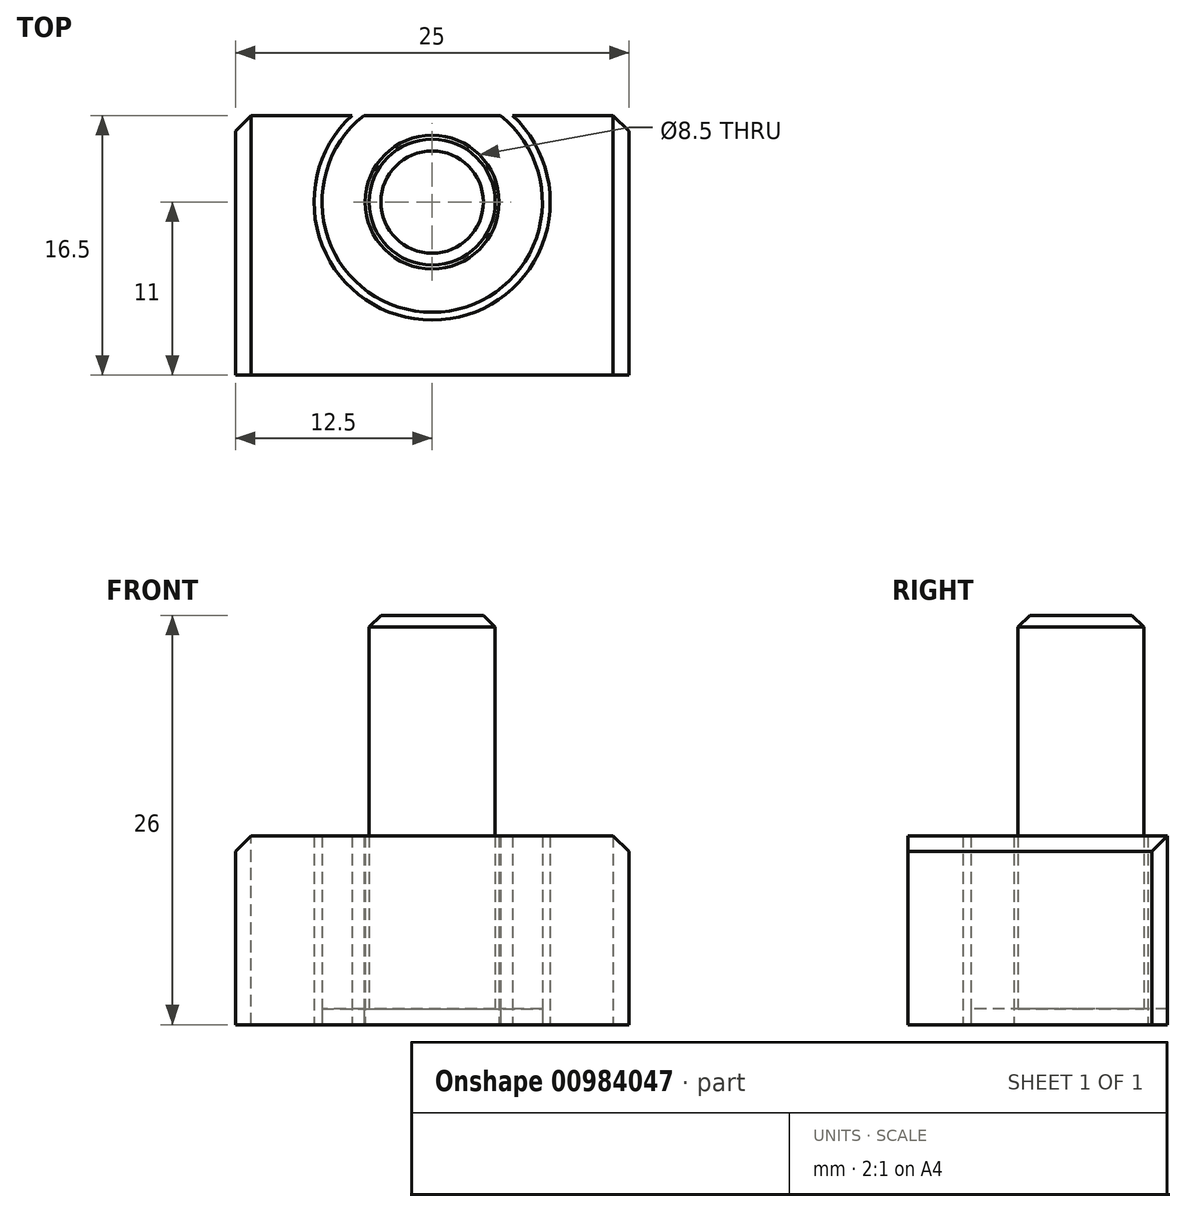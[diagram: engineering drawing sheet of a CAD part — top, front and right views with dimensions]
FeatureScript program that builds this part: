
annotation { "Feature Type Name" : "Feature", "Feature Type Description" : "" }
export const myFeature = defineFeature(function(context is Context, id is Id, definition is map)
    precondition{}
    {
        {
            var Q0;
            Q0=qCreatedBy(makeId("Top.planeOp"),FACE);
            var sketch = newSketch(context, id + "F0", { "sketchPlane" : qUnion([Q0])});
            skCircle(sketch, "E0", {"center": v(0, 0) * mm, "radius": 4 * mm});
            skCircle(sketch, "E1", {"center": v(0, 0) * mm, "radius": 4.25 * mm});
            skLineSegment(sketch, "E2.bottom", {"start": v(-12.5, 5.5) * mm, "end": v(12.5, 5.5) * mm});
            skLineSegment(sketch, "E2.top", {"start": v(-12.5, -11) * mm, "end": v(12.5, -11) * mm});
            skLineSegment(sketch, "E2.left", {"start": v(-12.5, 5.5) * mm, "end": v(-12.5, -11) * mm});
            skLineSegment(sketch, "E2.right", {"start": v(12.5, 5.5) * mm, "end": v(12.5, -11) * mm});
            skCircle(sketch, "E3", {"center": v(0, 0) * mm, "radius": 7.5 * mm});
            skCircle(sketch, "E4", {"center": v(0, 0) * mm, "radius": 7 * mm});
            skSolve(sketch);
        }
        {
            var Q0;
            Q0=makeQuery(id+"F0.imprint","IMPRINT",FACE,{"disambiguationData":[TD([[makeQuery(id+"F0.imprint","IMPRINT",EDGE,{"derivedFrom":sQuery(id+"F0.wireOp",EDGE,"E0")}),1.0]])]});
            extrude(context, id + "F1", {"entities" : qUnion([Q0]), "depth" : 26 * mm, "offsetDistance" : 25 * mm});
        }
        {
            var Q0;
            Q0=makeQuery(id+"F0.imprint","IMPRINT",FACE,{"disambiguationData":[TD([[makeQuery(id+"F0.imprint","IMPRINT",EDGE,{"derivedFrom":sQuery(id+"F0.wireOp",EDGE,"E1")}),-1.0]])]});
            var Q1;
            Q1=makeQuery(id+"F0.imprint","IMPRINT",FACE,{"disambiguationData":[TD([[makeQuery(id+"F0.imprint","IMPRINT",EDGE,{"derivedFrom":sQuery(id+"F0.wireOp",EDGE,"E0")}),1.0]])]});
            var Q2;
            Q2=makeQuery(id+"F0.imprint","IMPRINT",FACE,{"disambiguationData":[TD([[makeQuery(id+"F0.imprint","IMPRINT",EDGE,{"derivedFrom":sQuery(id+"F0.wireOp",EDGE,"E0")}),-1.0]])]});
            extrude(context, id + "F2", {"entities" : qUnion([Q0, Q1, Q2]), "operationType" : NewBodyOperationType.ADD, "depth" : 1 * mm, "offsetDistance" : 25 * mm});
        }
        {
            var Q0;
            Q0=makeQuery(id+"F0.imprint","IMPRINT",FACE,{"disambiguationData":[TD([[makeQuery(id+"F0.imprint","IMPRINT",EDGE,{"derivedFrom":sQuery(id+"F0.wireOp",EDGE,"E2.top")}),1.0]])]});
            var Q1;
            {var subQ0=sQuery(id+"F0.wireOp",EDGE,"E3");var subQ1=sQuery(id+"F0.wireOp",EDGE,"E2.bottom");var subQ2=makeQuery(id+"F0.imprint","INTERSECT",VERTEX,{"disambiguationData":[OD(0.0)],"derivedFrom":[subQ1,subQ0]});Q1=makeQuery(id+"F0.imprint","IMPRINT",FACE,{"disambiguationData":[TD([[makeQuery(id+"F0.imprint","IMPRINT",EDGE,{"disambiguationData":[TD([[subQ2,-1.0]])],"derivedFrom":subQ1}),-1.0]])]});}
            var Q2;
            Q2=makeQuery(id+"F0.imprint","IMPRINT",FACE,{"disambiguationData":[TD([[makeQuery(id+"F0.imprint","IMPRINT",EDGE,{"derivedFrom":sQuery(id+"F0.wireOp",EDGE,"E1")}),-1.0]])]});
            extrude(context, id + "F3", {"entities" : qUnion([Q0, Q1, Q2]), "depth" : 12 * mm, "offsetDistance" : 25 * mm});
        }
        {
            var Q0;
            Q0=makeQuery(id+"F1.opExtrude","CAP_EDGE",EDGE,{"disambiguationData":[OSD([sQuery(id+"F0.wireOp",EDGE,"E0")])],"isStart":false});
            chamfer(context, id + "F4", {"entities" : qUnion([Q0]), "width" : .75 * mm, "tangentPropagation" : true});
        }
        {
            var Q0;
            Q0=makeQuery(id+"F3.opExtrude","CAP_EDGE",EDGE,{"disambiguationData":[OSD([sQuery(id+"F0.wireOp",EDGE,"E2.right")])],"isStart":false});
            var Q1;
            Q1=makeQuery(id+"F3.opExtrude","CAP_EDGE",EDGE,{"disambiguationData":[OSD([sQuery(id+"F0.wireOp",EDGE,"E2.left")])],"isStart":false});
            var Q2;
            Q2=makeQuery(id+"F3.opExtrude","SWEPT_EDGE",EDGE,{"disambiguationData":[OSD([sQuery(id+"F0.wireOp",EDGE,"E2.bottom"),sQuery(id+"F0.wireOp",EDGE,"E2.right")])]});
            var Q3;
            Q3=makeQuery(id+"F3.opExtrude","SWEPT_EDGE",EDGE,{"disambiguationData":[OSD([sQuery(id+"F0.wireOp",EDGE,"E2.bottom"),sQuery(id+"F0.wireOp",EDGE,"E2.left")])]});
            chamfer(context, id + "F5", {"entities" : qUnion([Q0, Q1, Q2, Q3]), "width" : 1 * mm, "tangentPropagation" : true});
        }
    });
